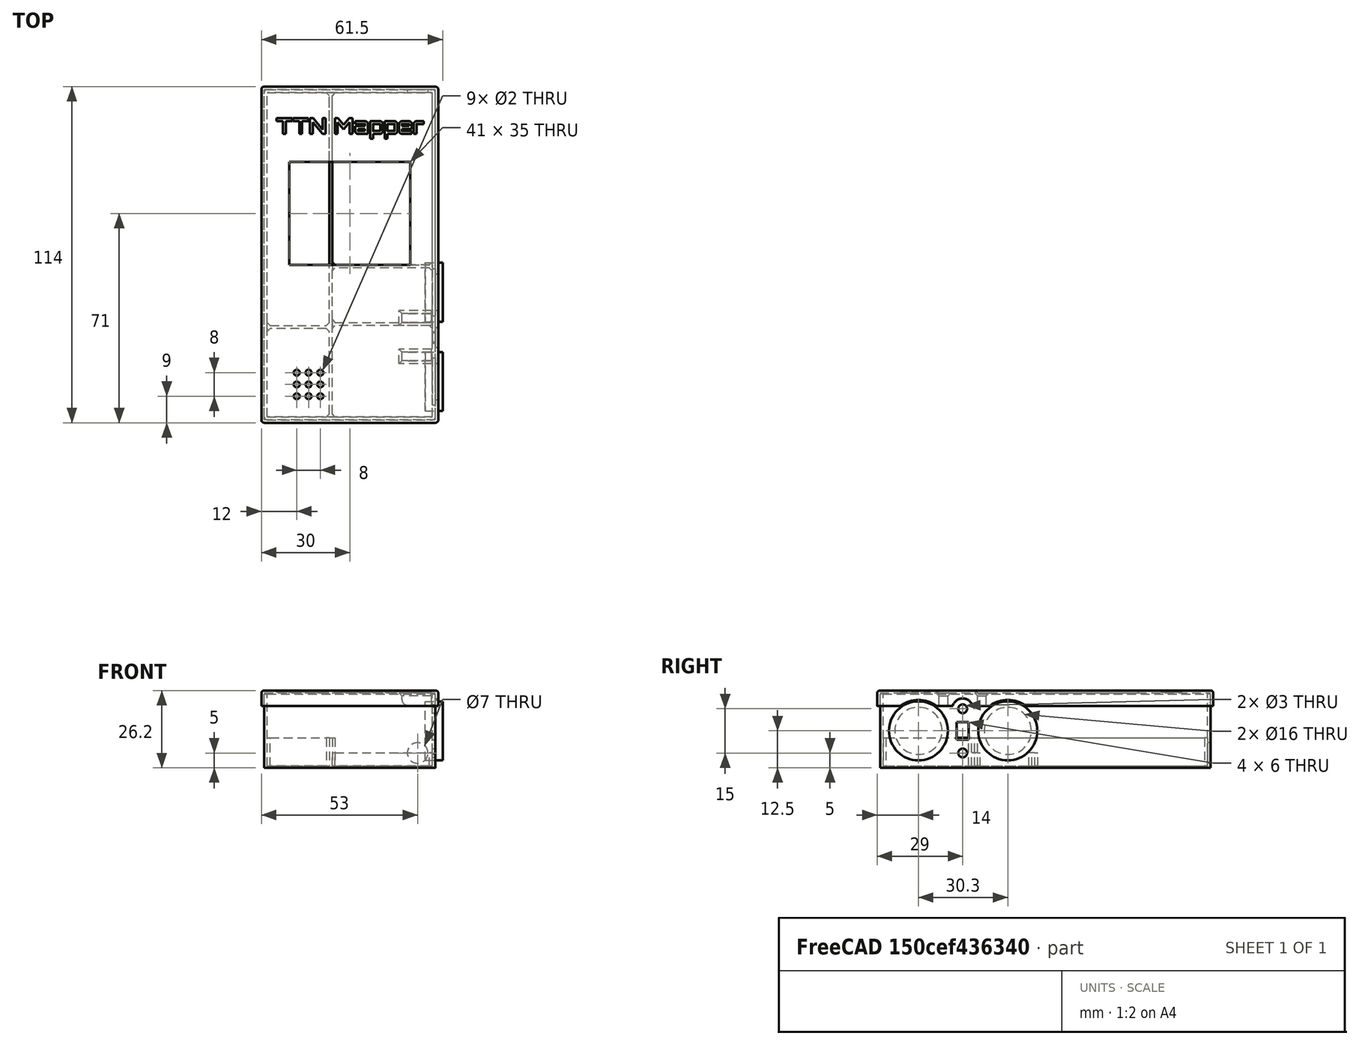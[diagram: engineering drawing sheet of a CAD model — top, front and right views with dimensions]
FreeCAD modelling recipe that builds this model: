
FCSTD DOCUMENT  (FreeCAD 0.17R13541 (Git))
Label: caja_LoRa+tapa_v3
License: CreativeCommons Attribution-ShareAlike
LicenseURL: http://creativecommons.org/licenses/by-sa/4.0/
objects: Part::Box×12, Part::Cylinder×11, Part::MultiFuse×6, Part::Cut×4, Part::Fillet×3, Part::Chamfer×2, Part::FeaturePython×1, Part::Part2DObjectPython×1, Part::Extrusion×1
note: 41 computed .brp shape members not serialized (recipe doc carries the construction recipe); baked Part::Feature solids carry a one-line shape summary decoded from their .brp

FEATURE [Part::Box] Box  label="Cubo_interior"
  AttacherType = Attacher::AttachEngine3D
  Height = 25
  Length = 56
  Placement = pos=(-28,-55,-11.9) rot=(0,0,1;0rad)
  Width = 110
FEATURE [Part::Box] Box001  label="Cubo_exterior"
  AttacherType = Attacher::AttachEngine3D
  Height = 25
  Length = 58
  Placement = pos=(-29,-56,-12.5) rot=(0,0,1;0rad)
  Width = 112
FEATURE [Part::Cut] Cut
  Base = -> Box001
  Refine = true
  Tool = -> Box
FEATURE [Part::Box] Box002  label="muro_pila"
  AttacherType = Attacher::AttachEngine3D
  Height = 10
  Length = 1
  Placement = pos=(-7,-56,-12.4) rot=(0,0,1;0rad)
  Width = 112
FEATURE [Part::Box] Box003  label="muro_lora"
  AttacherType = Attacher::AttachEngine3D
  Height = 5
  Length = 35.5
  Placement = pos=(-6.7,-4.5,-12.4) rot=(0,0,1;0rad)
  Width = 1
FEATURE [Part::Cylinder] Cylinder  label="antenna_hole"
  Angle = 360
  AttacherType = Attacher::AttachEngine3D
  Height = 50
  Placement = pos=(23,86.9,-7.5) rot=(1,0,0;1.5708rad)
  Radius = 3.5
FEATURE [Part::Cylinder] Cylinder001  label="boton1"
  Angle = 360
  AttacherType = Attacher::AttachEngine3D
  Height = 6
  Placement = pos=(25.5,-12.7,0) rot=(0,1,0;1.5708rad)
  Radius = 8
FEATURE [Part::Cylinder] Cylinder002  label="boton2"
  Angle = 360
  AttacherType = Attacher::AttachEngine3D
  Height = 6
  Placement = pos=(25.5,-43,0) rot=(0,1,0;1.5708rad)
  Radius = 8
FEATURE [Part::Cylinder] Cylinder003  label="boton1_out"
  Angle = 360
  AttacherType = Attacher::AttachEngine3D
  Height = 6
  Placement = pos=(25.5,-12.7,0) rot=(0,1,0;1.5708rad)
  Radius = 10
FEATURE [Part::Cylinder] Cylinder004  label="boton2_out"
  Angle = 360
  AttacherType = Attacher::AttachEngine3D
  Height = 6
  Placement = pos=(25.5,-43,0) rot=(0,1,0;1.5708rad)
  Radius = 10
FEATURE [Part::Box] Box004  label="muro_botones"
  AttacherType = Attacher::AttachEngine3D
  Height = 5
  Length = 35.5
  Placement = pos=(-6.7,-24,-12.4) rot=(0,0,1;0rad)
  Width = 1
FEATURE [Part::Box] Box005  label="interruptor"
  AttacherType = Attacher::AttachEngine3D
  Height = 6
  Length = 10
  Placement = pos=(24,-30,-3) rot=(0,0,1;0rad)
  Width = 4
FEATURE [Part::Cylinder] Cylinder005  label="tornillo_1"
  Angle = 360
  AttacherType = Attacher::AttachEngine3D
  Height = 20
  Placement = pos=(19.5,-28,-7.5) rot=(0,1,0;1.5708rad)
  Radius = 1.5
FEATURE [Part::Cylinder] Cylinder006  label="tornillo_2"
  Angle = 360
  AttacherType = Attacher::AttachEngine3D
  Height = 20
  Placement = pos=(19.5,-28,7.5) rot=(0,1,0;1.5708rad)
  Radius = 1.5
FEATURE [Part::Box] Box006  label="muro_bateria"
  AttacherType = Attacher::AttachEngine3D
  Height = 10
  Length = 22
  Placement = pos=(-28,-25,-12.4) rot=(0,0,1;0rad)
  Width = 1
FEATURE [Part::MultiFuse] Fusion  label="muros"
  Refine = true
  Shapes = -> [Box002,Box003,Box004,Box006]
FEATURE [Part::MultiFuse] Fusion001  label="cortes"
  Refine = true
  Shapes = -> [Cylinder006,Cylinder005,Box005,Cylinder002,Cylinder001,Cylinder]
FEATURE [Part::MultiFuse] Fusion002
  Refine = true
  Shapes = -> [Cut,Fusion]
FEATURE [Part::Cut] Cut001
  Base = -> Fusion002
  Refine = true
  Tool = -> Fusion001
FEATURE [Part::Chamfer] Chamfer
  Base = -> Cut001
  Edges = 16 edges r=1: [Edge29,Edge31,Edge34,Edge38,Edge39,Edge42,Edge52,Edge56,Edge59,Edge61,Edge75,Edge81,Edge83,Edge85,Edge87,Edge99]
FEATURE [Part::Fillet] Fillet  label="base_caja_lora"
  Base = -> Chamfer
  Edges = 4 edges r=1: [Edge107,Edge108,Edge111,Edge114]
FEATURE [Part::Box] Box007  label="corte_Tapa_interior"
  AttacherType = Attacher::AttachEngine3D
  Height = 25
  Length = 58
  Placement = pos=(-29,-56,-12.1) rot=(0,0,1;0rad)
  Width = 112
FEATURE [Part::Box] Box008  label="Tapa_exterior"
  AttacherType = Attacher::AttachEngine3D
  Height = 5.2
  Length = 60
  Placement = pos=(-30,-57,8.5) rot=(0,0,1;0rad)
  Width = 114
FEATURE [Part::Cylinder] Cylinder007  label="corte_boton003"
  Angle = 360
  AttacherType = Attacher::AttachEngine3D
  Height = 6
  Placement = pos=(25.5,-12.7,0) rot=(0,1,0;1.5708rad)
  Radius = 10.5
FEATURE [Part::Cylinder] Cylinder008  label="corte_boton004"
  Angle = 360
  AttacherType = Attacher::AttachEngine3D
  Height = 6
  Placement = pos=(25.5,-43,0) rot=(0,1,0;1.5708rad)
  Radius = 10.5
FEATURE [Part::Cylinder] Cylinder009  label="corte_tornillo_003"
  Angle = 360
  AttacherType = Attacher::AttachEngine3D
  Height = 20
  Placement = pos=(19.5,-28,7.5) rot=(0,1,0;1.5708rad)
  Radius = 3.5
FEATURE [Part::Box] Box009  label="corte_LCD"
  AttacherType = Attacher::AttachEngine3D
  Height = 10
  Length = 41
  Placement = pos=(-20.5,-3.5,7) rot=(0,0,1;0rad)
  Width = 35
FEATURE [Part::Cylinder] Cylinder010  label="Cylinder"
  Angle = 360
  AttacherType = Attacher::AttachEngine3D
  Height = 10
  Placement = pos=(-18,-48,8) rot=(0,0,1;0rad)
  Radius = 1
FEATURE [Part::FeaturePython] Array  label="corte_beep"  # Draft array (typed FeaturePython)
  Angle = 360
  ArrayType = 0
  Axis = (0,0,1)
  Base = -> Cylinder010
  Center = (0,0,0)
  Fuse = false
  IntervalAxis = (0,0,0)
  IntervalX = (4,0,0)
  IntervalY = (0,4,0)
  IntervalZ = (0,0,0)
  NumberPolar = 2
  NumberX = 3
  NumberY = 3
  NumberZ = 2
FEATURE [Part::MultiFuse] Fusion003  label="corte_tapa"
  Refine = true
  Shapes = -> [Array,Box007,Cylinder009,Cylinder008,Cylinder007,Box009]
FEATURE [Part::Cut] Cut002
  Base = -> Box008
  Refine = true
  Tool = -> Fusion003
FEATURE [Part::Box] Box010  label="contrafuerte"
  AttacherType = Attacher::AttachEngine3D
  Height = 5
  Length = 10
  Placement = pos=(17.7,-23,8.6) rot=(0,0,1;0rad)
  Width = 3
FEATURE [Part::Box] Box011  label="contrafuerte001"
  AttacherType = Attacher::AttachEngine3D
  Height = 5
  Length = 10
  Placement = pos=(17.7,-36,8.6) rot=(0,0,1;0rad)
  Width = 3
FEATURE [Part::MultiFuse] Fusion004  label="contrafuertes"
  Refine = true
  Shapes = -> [Box010,Box011]
FEATURE [Part::MultiFuse] Fusion005
  Refine = true
  Shapes = -> [Cut002,Fusion004]
FEATURE [Part::Chamfer] Chamfer001
  Base = -> Fusion005
  Edges = 6 edges r=1: [Edge82,Edge84,Edge85,Edge86,Edge88,Edge89]
FEATURE [Part::Fillet] Fillet001
  Base = -> Chamfer001
  Edges = 2 edges r=2: [Edge92,Edge117]
FEATURE [Part::Fillet] Fillet002
  Base = -> Fillet001
  Edges = 8 edges r=1: [Edge114,Edge115,Edge116,Edge117,Edge126,Edge127,Edge128,Edge129]
FEATURE [Part::Part2DObjectPython] ShapeString  # Draft 2D object (typed FeaturePython)
  FontFile = <userpath>/Dropbox/3D/diseños/Orbitron/Orbitron-Bold.ttf
  Placement = pos=(-19,-12,0) rot=(0,0,1;0rad)
  Size = 2.4
  String = TTN Mapper
  Tracking = 0
FEATURE [Part::Extrusion] Extrude  label="TTNMAPER TEXT"
  Base = -> ShapeString
  Dir = (0,0,1)
  DirMode = 0
  FaceMakerClass = Part::FaceMakerBullseye
  LengthFwd = 2
  LengthRev = 0
  Placement = pos=(-6,53,13.2) rot=(0,0,1;0rad)
  Solid = true
  Symmetric = false
FEATURE [Part::Cut] Cut003  label="Tapa_final"
  Base = -> Fillet002
  Refine = true
  Tool = -> Extrude
